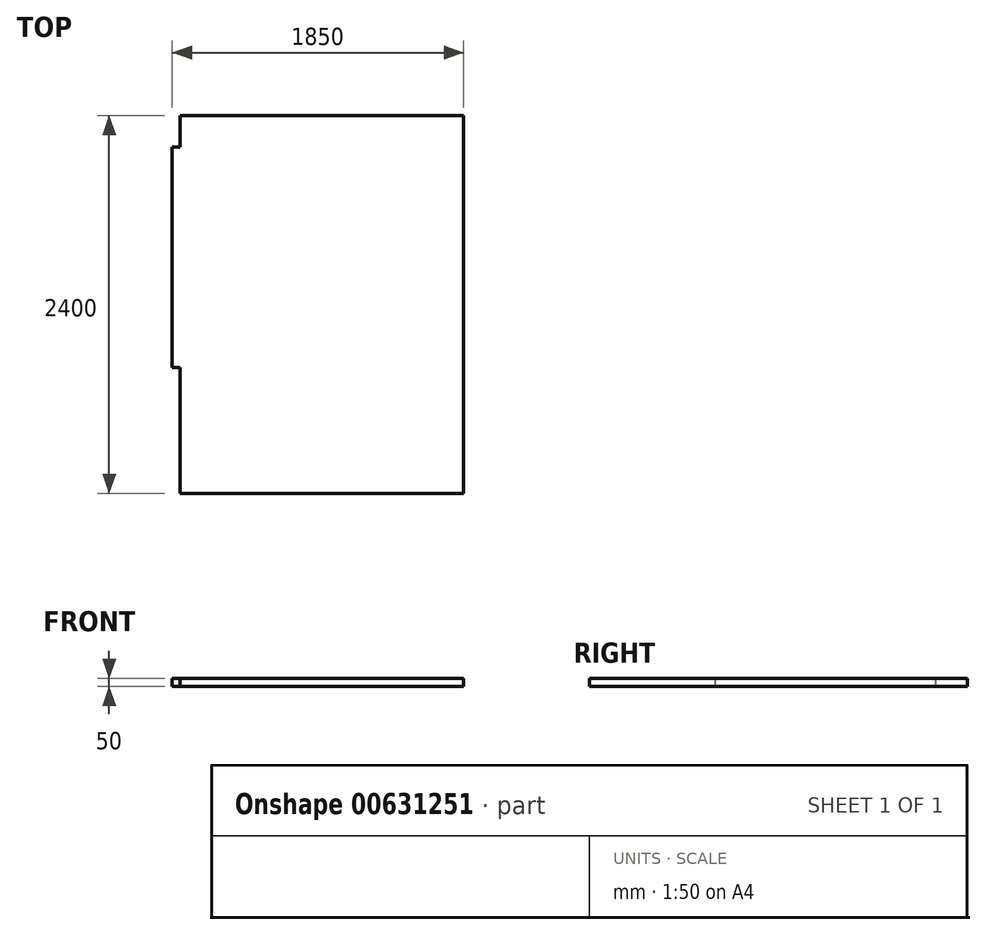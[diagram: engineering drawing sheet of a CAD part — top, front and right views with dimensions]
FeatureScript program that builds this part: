
annotation { "Feature Type Name" : "Feature", "Feature Type Description" : "" }
export const myFeature = defineFeature(function(context is Context, id is Id, definition is map)
    precondition{}
    {
        {
            var Q0;
            Q0=qCreatedBy(makeId("Top.planeOp"),FACE);
            var sketch = newSketch(context, id + "F0", { "sketchPlane" : qUnion([Q0])});
            skLineSegment(sketch, "E0.bottom", {"start": v(-1455.4, 1170.56) * mm, "end": v(344.6, 1170.56) * mm});
            skLineSegment(sketch, "E0.top", {"start": v(-1455.4, -1229.44) * mm, "end": v(344.6, -1229.44) * mm});
            skLineSegment(sketch, "E0.left", {"start": v(-1455.4, 1170.56) * mm, "end": v(-1455.4, -1229.44) * mm});
            skLineSegment(sketch, "E0.right", {"start": v(344.6, 1170.56) * mm, "end": v(344.6, -1229.44) * mm});
            skSolve(sketch);
        }
        {
            var Q0;
            Q0=makeQuery(id+"F0.imprint","IMPRINT",FACE,{"disambiguationData":[TD([[makeQuery(id+"F0.imprint","IMPRINT",EDGE,{"derivedFrom":sQuery(id+"F0.wireOp",EDGE,"E0.bottom")}),-1.0]])]});
            extrude(context, id + "F1", {"entities" : qUnion([Q0]), "depth" : 50 * mm, "offsetDistance" : 25 * mm});
        }
        {
            var Q0;
            Q0=makeQuery(id+"F1.opExtrude","SWEPT_FACE",FACE,{"disambiguationData":[OSD([sQuery(id+"F0.wireOp",EDGE,"E0.left")])]});
            var sketch = newSketch(context, id + "F2", { "sketchPlane" : qUnion([Q0])});
            skLineSegment(sketch, "E1.bottom", {"start": v(-970.56, 0) * mm, "end": v(429.44, 0) * mm});
            skLineSegment(sketch, "E1.top", {"start": v(-970.56, 50) * mm, "end": v(429.44, 50) * mm});
            skLineSegment(sketch, "E1.left", {"start": v(-970.56, 0) * mm, "end": v(-970.56, 50) * mm});
            skLineSegment(sketch, "E1.right", {"start": v(429.44, 0) * mm, "end": v(429.44, 50) * mm});
            skSolve(sketch);
        }
        {
            var Q0;
            Q0=makeQuery(id+"F2.imprint","IMPRINT",FACE,{"disambiguationData":[TD([[makeQuery(id+"F2.imprint","IMPRINT",EDGE,{"derivedFrom":sQuery(id+"F2.wireOp",EDGE,"E1.bottom")}),1.0]])]});
            extrude(context, id + "F3", {"entities" : qUnion([Q0]), "operationType" : NewBodyOperationType.ADD, "depth" : 50 * mm, "offsetDistance" : 25 * mm});
        }
    });
